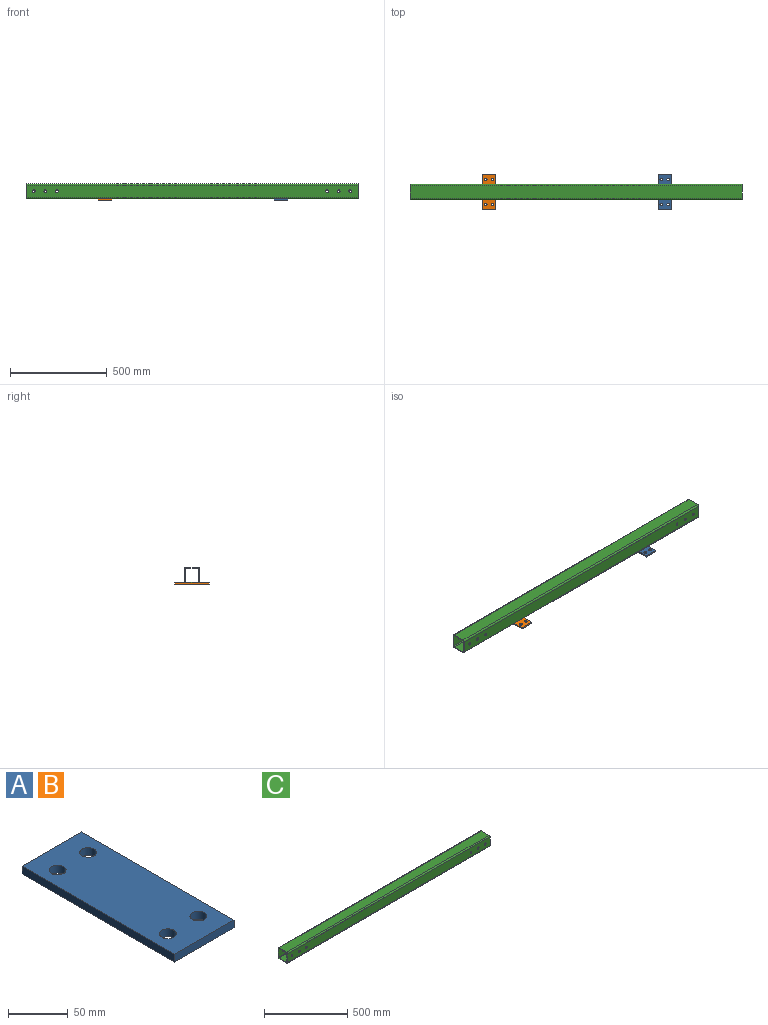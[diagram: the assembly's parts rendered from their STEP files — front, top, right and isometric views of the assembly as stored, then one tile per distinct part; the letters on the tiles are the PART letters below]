
ASSEMBLY  parts=3 mates=2
PART A: 10 faces, bbox 70x180x8 mm
  f0: plane 180x8mm, normal (-1,0,0), area 1440mm2, adj f1,f3,f4,f5
  f1: plane 70x8mm, normal (0,-1,0), area 560mm2, adj f0,f2,f4,f5
  f2: plane 180x8mm, normal (1,0,0), area 1440mm2, adj f1,f3,f4,f5
  f3: plane 70x8mm, normal (0,1,0), area 560mm2, adj f0,f2,f4,f5
  f4: plane 180x70mm, normal (0,0,-1), area 11984.2mm2, adj f0,f1,f2,f3,f6,f7,f8,f9
  f5: plane 180x70mm, normal (0,0,1), area 11984.2mm2, adj f0,f1,f2,f3,f6,f7,f8,f9
  f6: cylinder r=7mm len=14mm, axis (0,0,1), area 351.9mm2, adj f4,f5
  f7: cylinder r=7mm len=14mm, axis (0,0,1), area 351.9mm2, adj f4,f5
  f8: cylinder r=7mm len=14mm, axis (0,0,1), area 351.9mm2, adj f4,f5
  f9: cylinder r=7mm len=14mm, axis (0,0,1), area 351.9mm2, adj f4,f5
PART B: same geometry as A
PART C: 30 faces, bbox 1720x80x80 mm
  f0: plane 80x80mm, normal (1,0,0), area 1174.8mm2, adj f2,f3,f4,f5,f6,f7,f8,f9
  f1: plane 80x80mm, normal (-1,0,0), area 1174.8mm2, adj f2,f3,f4,f5,f6,f7,f8,f9
  f2: plane 1720x64mm, normal (0,0,1), area 110080mm2, adj f0,f1,f3,f9
  f3: cylinder r=8mm len=1720mm, axis (-1,0,0), area 21614.2mm2, adj f0,f1,f2,f4
  f4: plane 1720x64mm, normal (0,-1,0), area 109156.4mm2, adj f0,f1,f3,f5,f24,f25,f26,f27
  f5: cylinder r=8mm len=1720mm, axis (-1,0,0), area 21614.2mm2, adj f0,f1,f4,f6
  f6: plane 1720x64mm, normal (0,0,-1), area 110080mm2, adj f0,f1,f5,f7
  f7: cylinder r=8mm len=1720mm, axis (-1,0,0), area 21614.2mm2, adj f0,f1,f6,f8
  f8: plane 1720x64mm, normal (0,1,0), area 109156.4mm2, adj f0,f1,f7,f9,f18,f19,f20,f21
  f9: cylinder r=8mm len=1720mm, axis (-1,0,0), area 21614.2mm2, adj f0,f1,f2,f8
  f10: plane 1720x64mm, normal (0,0,-1), area 110080mm2, adj f0,f1,f11,f17
  f11: cylinder r=4mm len=1720mm, axis (-1,0,0), area 10807.1mm2, adj f0,f1,f10,f12
  f12: plane 1720x64mm, normal (0,1,0), area 109156.4mm2, adj f0,f1,f11,f13,f24,f25,f26,f27
  f13: cylinder r=4mm len=1720mm, axis (-1,0,0), area 10807.1mm2, adj f0,f1,f12,f14
  f14: plane 1720x64mm, normal (0,0,1), area 110080mm2, adj f0,f1,f13,f15
  f15: cylinder r=4mm len=1720mm, axis (-1,0,0), area 10807.1mm2, adj f0,f1,f14,f16
  f16: plane 1720x64mm, normal (0,-1,0), area 109156.4mm2, adj f0,f1,f15,f17,f18,f19,f20,f21
  f17: cylinder r=4mm len=1720mm, axis (-1,0,0), area 10807.1mm2, adj f0,f1,f10,f16
  f18: cylinder r=7mm len=14mm, axis (0,-1,0), area 175.9mm2, adj f8,f16
  f19: cylinder r=7mm len=14mm, axis (0,-1,0), area 175.9mm2, adj f8,f16
  f20: cylinder r=7mm len=14mm, axis (0,-1,0), area 175.9mm2, adj f8,f16
  f21: cylinder r=7mm len=14mm, axis (0,-1,0), area 175.9mm2, adj f8,f16
  f22: cylinder r=7mm len=14mm, axis (0,-1,0), area 175.9mm2, adj f8,f16
  f23: cylinder r=7mm len=14mm, axis (0,-1,0), area 175.9mm2, adj f8,f16
  f24: cylinder r=7mm len=14mm, axis (0,-1,0), area 175.9mm2, adj f4,f12
  f25: cylinder r=7mm len=14mm, axis (0,-1,0), area 175.9mm2, adj f4,f12
  f26: cylinder r=7mm len=14mm, axis (0,-1,0), area 175.9mm2, adj f4,f12
  f27: cylinder r=7mm len=14mm, axis (0,-1,0), area 175.9mm2, adj f4,f12
  f28: cylinder r=7mm len=14mm, axis (0,-1,0), area 175.9mm2, adj f4,f12
  f29: cylinder r=7mm len=14mm, axis (0,-1,0), area 175.9mm2, adj f4,f12
PLACE A t=(65.8,84.22,-67.31)mm
PLACE B t=(-844.2,84.22,-67.31)mm
PLACE C t=(-1219.2,134.22,-67.31)mm
MATE fastened B.f5 <-> C.f6  axis (0,0,1) through (-809.2,174.22,-67.31)mm
MATE fastened A.f5 <-> C.f6  axis (0,0,1) through (100.8,174.22,-67.31)mm
